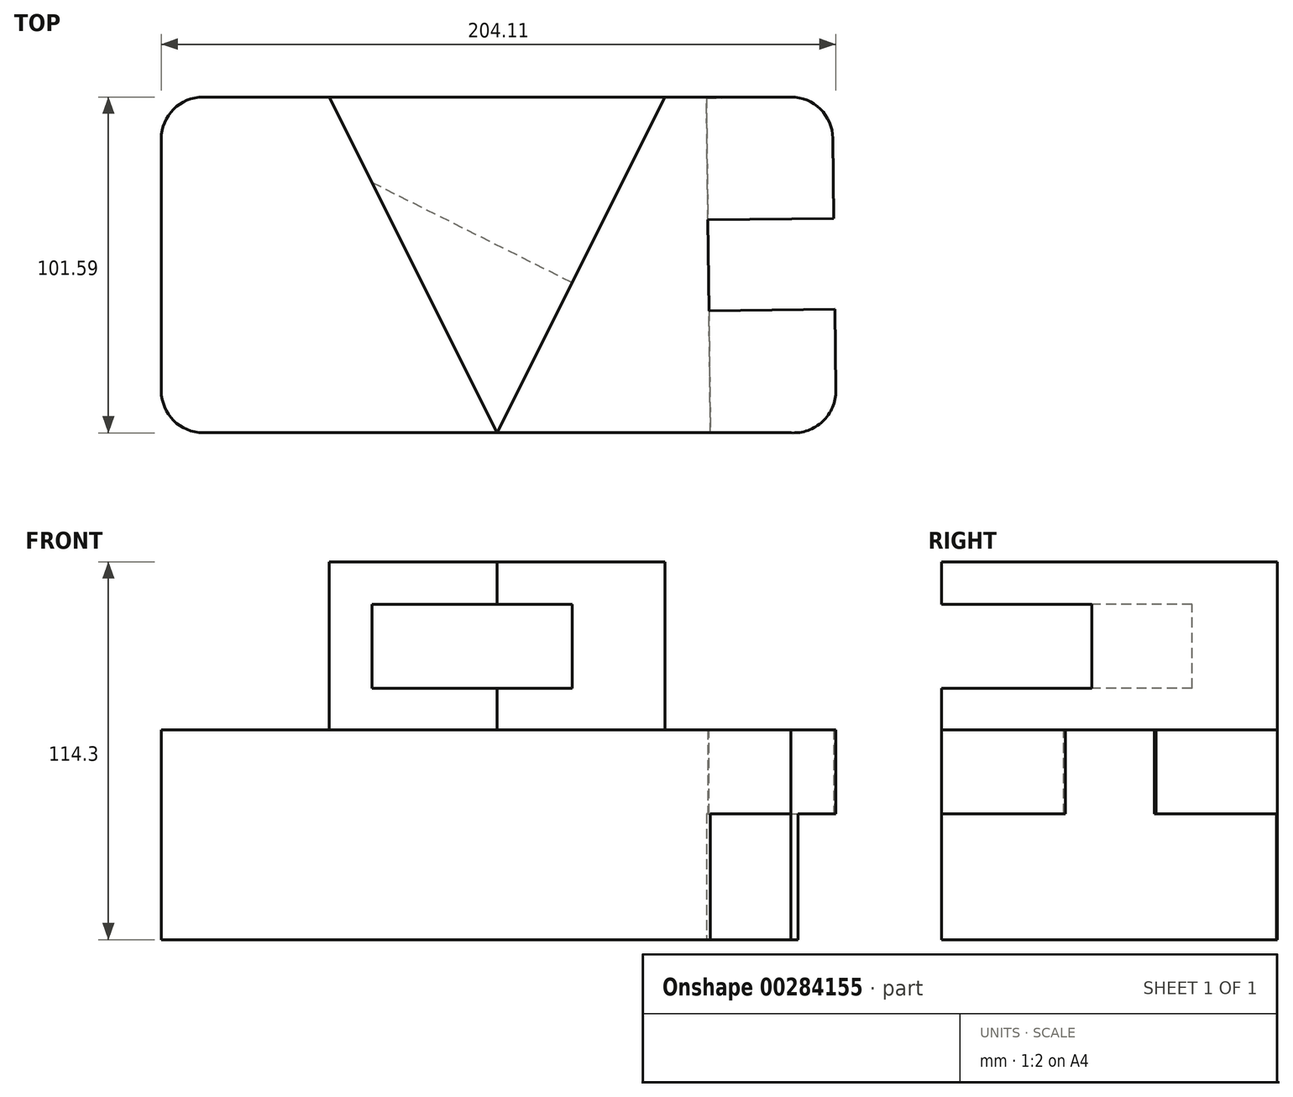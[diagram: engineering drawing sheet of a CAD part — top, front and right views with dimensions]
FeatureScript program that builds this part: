
annotation { "Feature Type Name" : "Feature", "Feature Type Description" : "" }
export const myFeature = defineFeature(function(context is Context, id is Id, definition is map)
    precondition{}
    {
        {
            var Q0;
            Q0=qCreatedBy(makeId("Top.planeOp"),FACE);
            var sketch = newSketch(context, id + "F0", { "sketchPlane" : qUnion([Q0])});
            skLineSegment(sketch, "E0", {"start": v(0, 0) * mm, "end": v(-177.8, 0) * mm});
            skArc(sketch, "E1", {"start": v(-177.8, 0) * mm, "mid": v(-186.77, 3.7) * mm, "end": v(-190.5, 12.66) * mm});
            skLineSegment(sketch, "E2", {"start": v(-190.5, 12.66) * mm, "end": v(-190.5, 88.86) * mm});
            skArc(sketch, "E3", {"start": v(-190.5, 88.86) * mm, "mid": v(-186.78, 97.84) * mm, "end": v(-177.8, 101.56) * mm});
            skLineSegment(sketch, "E4", {"start": v(-177.8, 101.56) * mm, "end": v(0, 101.56) * mm});
            skArc(sketch, "E5", {"start": v(0, 101.56) * mm, "mid": v(8.93, 97.9) * mm, "end": v(12.7, 89.01) * mm});
            skLineSegment(sketch, "E6", {"start": v(12.7, 89.01) * mm, "end": v(13.6, 12.82) * mm});
            skArc(sketch, "E7", {"start": v(13.6, 12.82) * mm, "mid": v(9.62, 3.42) * mm, "end": v(0, 0) * mm});
            skSolve(sketch);
        }
        {
            var Q0;
            Q0 = qSketchRegion(id + "F0", true);
            extrude(context, id + "F1", {"entities" : qUnion([Q0]), "oppositeDirection" : true, "depth" : 50.8 * mm});
        }
        {
            var Q0;
            Q0=makeQuery(id+"F1.opExtrude","CAP_FACE",FACE,{"disambiguationData":[OSD([sQuery(id+"F0.wireOp",EDGE,"E0"),sQuery(id+"F0.wireOp",EDGE,"E1"),sQuery(id+"F0.wireOp",EDGE,"E2"),sQuery(id+"F0.wireOp",EDGE,"E3"),sQuery(id+"F0.wireOp",EDGE,"E4"),sQuery(id+"F0.wireOp",EDGE,"E5"),sQuery(id+"F0.wireOp",EDGE,"E6"),sQuery(id+"F0.wireOp",EDGE,"E7")])],"isStart":true});
            var sketch = newSketch(context, id + "F2", { "sketchPlane" : qUnion([Q0])});
            skLineSegment(sketch, "E8", {"start": v(-139.7, 101.56) * mm, "end": v(-38.1, 101.56) * mm});
            skLineSegment(sketch, "E9", {"start": v(-38.1, 101.56) * mm, "end": v(-88.9, 0) * mm});
            skLineSegment(sketch, "E10", {"start": v(-88.9, 0) * mm, "end": v(-139.7, 101.56) * mm});
            skSolve(sketch);
        }
        {
            var Q0;
            Q0 = qSketchRegion(id + "F2", true);
            var Q1;
            Q1=makeQuery(id+"F1.opExtrude","CAP_FACE",FACE,{"disambiguationData":[OSD([sQuery(id+"F0.wireOp",EDGE,"E0"),sQuery(id+"F0.wireOp",EDGE,"E1"),sQuery(id+"F0.wireOp",EDGE,"E2"),sQuery(id+"F0.wireOp",EDGE,"E3"),sQuery(id+"F0.wireOp",EDGE,"E4"),sQuery(id+"F0.wireOp",EDGE,"E5"),sQuery(id+"F0.wireOp",EDGE,"E6"),sQuery(id+"F0.wireOp",EDGE,"E7")])],"isStart":false});
            extrude(context, id + "F3", {"entities" : qUnion([Q0, Q1]), "operationType" : NewBodyOperationType.ADD, "depth" : 63.5 * mm});
        }
        {
            var Q0;
            Q0=makeQuery(id+"F3.opExtrude","SWEPT_FACE",FACE,{"disambiguationData":[OSD([sQuery(id+"F2.wireOp",EDGE,"E9")])]});
            var sketch = newSketch(context, id + "F4", { "sketchPlane" : qUnion([Q0])});
            skLineSegment(sketch, "E11.bottom", {"start": v(-39.77, 50.63) * mm, "end": v(11.03, 50.63) * mm});
            skLineSegment(sketch, "E11.top", {"start": v(-39.77, 25.23) * mm, "end": v(11.03, 25.23) * mm});
            skLineSegment(sketch, "E11.left", {"start": v(-39.77, 50.63) * mm, "end": v(-39.77, 25.23) * mm});
            skLineSegment(sketch, "E11.right", {"start": v(11.03, 50.63) * mm, "end": v(11.03, 25.23) * mm});
            skSolve(sketch);
        }
        {
            var Q0;
            Q0=makeQuery(id+"F4.imprint","IMPRINT",FACE,{"disambiguationData":[TD([[makeQuery(id+"F4.imprint","IMPRINT",EDGE,{"derivedFrom":sQuery(id+"F4.wireOp",EDGE,"E11.bottom")}),-1.0]])]});
            extrude(context, id + "F5", {"entities" : qUnion([Q0]), "operationType" : NewBodyOperationType.REMOVE, "endBound" : BoundingType.THROUGH_ALL, "oppositeDirection" : true, "depth" : 25.4 * mm});
        }
        {
            var Q0;
            {var subQ0=sQuery(id+"F0.wireOp",EDGE,"E6");Q0=makeQuery(id+"F3.boolean.opBoolean","MERGE",FACE,{"derivedFrom":[makeQuery(id+"F1.opExtrude","SWEPT_FACE",FACE,{"disambiguationData":[OSD([subQ0])]}),makeQuery(id+"F3.opExtrude","SWEPT_FACE",FACE,{"disambiguationData":[OSD([subQ0])]})]});}
            var sketch = newSketch(context, id + "F6", { "sketchPlane" : qUnion([Q0])});
            skLineSegment(sketch, "E12", {"start": v(37.22, 12.7) * mm, "end": v(64.68, 12.7) * mm});
            skLineSegment(sketch, "E13", {"start": v(64.68, 12.7) * mm, "end": v(64.68, -12.7) * mm});
            skLineSegment(sketch, "E14", {"start": v(64.68, -12.7) * mm, "end": v(101.55, -12.7) * mm});
            skLineSegment(sketch, "E15", {"start": v(101.55, -12.7) * mm, "end": v(101.55, -50.8) * mm});
            skLineSegment(sketch, "E16", {"start": v(101.55, -50.8) * mm, "end": v(0, -50.8) * mm});
            skLineSegment(sketch, "E17", {"start": v(0, -50.8) * mm, "end": v(0, 0) * mm});
            skLineSegment(sketch, "E18", {"start": v(-1.2, -12.7) * mm, "end": v(37.22, -12.7) * mm});
            skLineSegment(sketch, "E19", {"start": v(37.22, -12.7) * mm, "end": v(37.22, 12.7) * mm});
            skSolve(sketch);
        }
        {
            var Q0;
            {var subQ0=sQuery(id+"F6.wireOp",EDGE,"E15");Q0=makeQuery(id+"F6.imprint","IMPRINT",FACE,{"disambiguationData":[TD([[makeQuery(id+"F6.imprint","IMPRINT",EDGE,{"derivedFrom":subQ0}),-1.0]])]});}
            var Q1;
            {var subQ0=sQuery(id+"F6.wireOp",EDGE,"E16");var subQ5=sQuery(id+"F6.wireOp",EDGE,"E17");var subQ6=makeQuery(id+"F6.imprint","INTERSECT",VERTEX,{"derivedFrom":[subQ0,subQ5]});Q1=makeQuery(id+"F6.imprint","IMPRINT",FACE,{"disambiguationData":[TD([[makeQuery(id+"F6.imprint","IMPRINT",EDGE,{"disambiguationData":[TD([[subQ6,-1.0]])],"derivedFrom":subQ5}),-1.0]])]});}
            var Q2;
            Q2=makeQuery(id+"F6.imprint","IMPRINT",FACE,{"disambiguationData":[TD([[makeQuery(id+"F6.imprint","IMPRINT",EDGE,{"derivedFrom":sQuery(id+"F6.wireOp",EDGE,"E12")}),1.0]])]});
            extrude(context, id + "F7", {"entities" : qUnion([Q0, Q1, Q2]), "operationType" : NewBodyOperationType.REMOVE, "oppositeDirection" : true, "depth" : 38.1 * mm});
        }
    });
